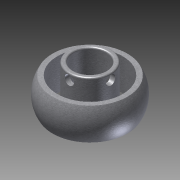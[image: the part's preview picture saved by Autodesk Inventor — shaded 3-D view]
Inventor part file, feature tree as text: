
AUTODESK INVENTOR PART (.ipt)
format: ipt  version: 2012 (Build 160160000, 160)  size: 183,296 bytes
history: native  units: mm
features: sketch x5, extrude x4, fillet x1, revolve x1, plane x1
ambient origin geometry x8: Origin, YZ Plane, XZ Plane, XY Plane, X Axis, Y Axis, Z Axis, Center Point
bodies: Solid1 (feature_tree)
feature tree (12):
  sketch  "Sketch1"  dims[d0=48.0mm d1=3.0mm]
  extrude  "Extrusion1"  Depth=3.0mm
  extrude  "Extrusion2"  Depth=3.0mm
  extrude  "Extrusion3"  Depth=28.5mm TaperAngle=0.0deg
  extrude  "Extrusion4"  Depth=6.0mm
  fillet  "Fillet1"  Radius=28.5mm
  revolve  "Revolution1"  [1 undecoded]
  plane  "Work Plane1"
  sketch  "Sketch5"  dims[d14=4.0mm d15=6.0mm d16=28.5mm d17=0.0mm d18=1.0mm d19=20.0mm d20=90.0deg]
  sketch  "Sketch2"  dims[d2=21.0mm d3=3.0mm]
  sketch  "Sketch3"  dims[d4=20.5mm d5=0.0mm d6=28.5mm d7=4.0mm d8=0.0mm d9=0.0mm]
  sketch  "Sketch4"  dims[d10=4.0mm d11=6.0mm d12=28.5mm d13=0.0mm]
note: 1 required parameter value undecoded (feature->parameter linkage not recoverable at this tier; creation-order binding heuristic only, values carry confidence <= 0.55)
